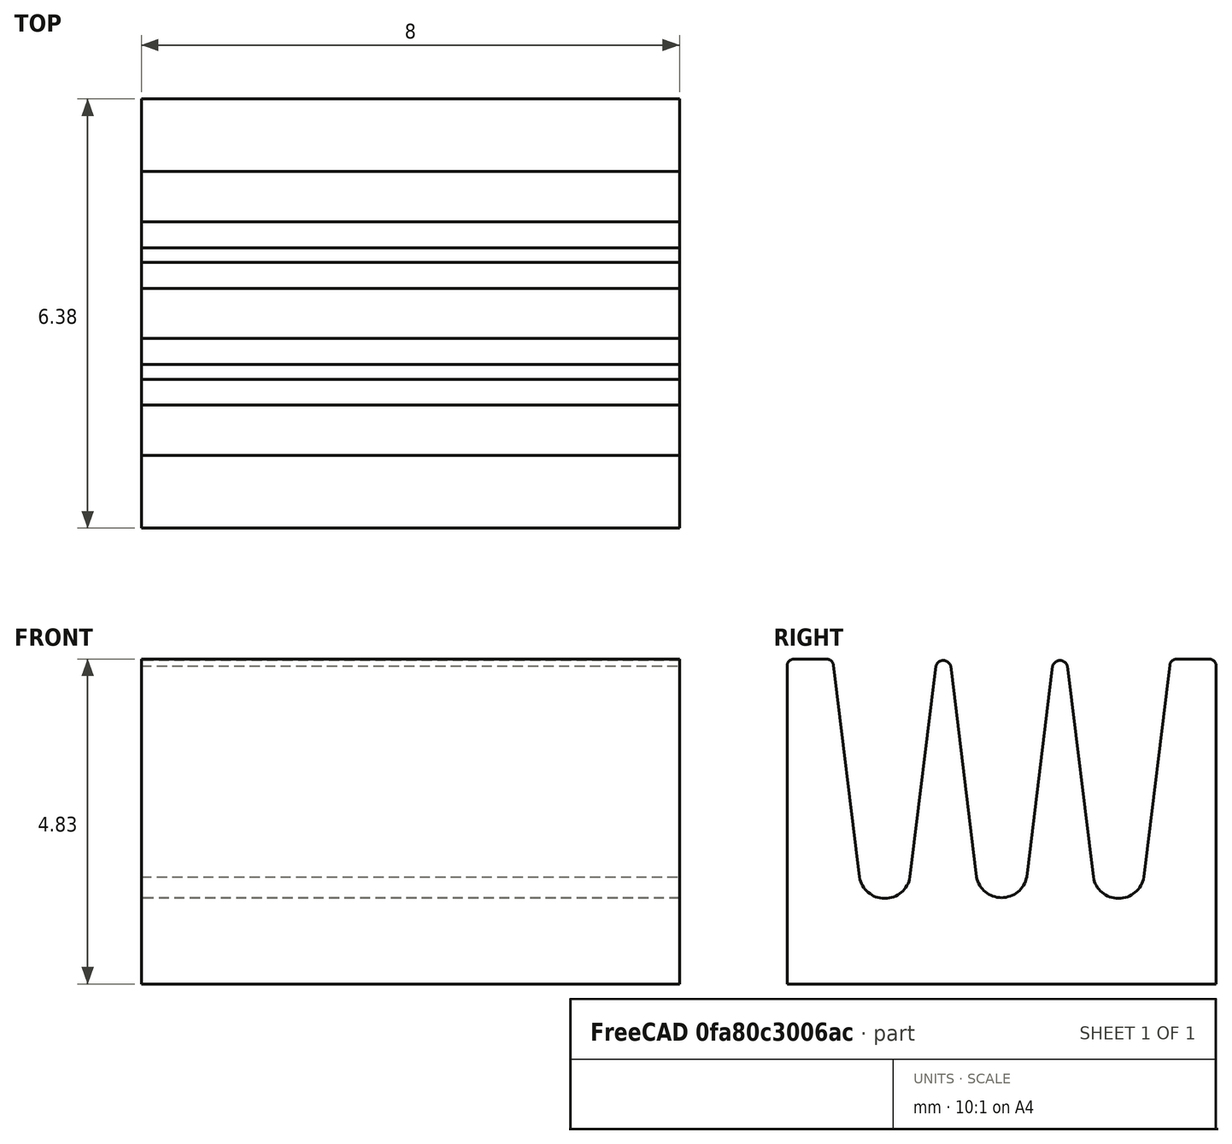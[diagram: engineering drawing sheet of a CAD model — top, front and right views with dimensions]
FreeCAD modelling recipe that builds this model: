
FCSTD DOCUMENT  (FreeCAD 0.18R4 (GitTag))
Label: heat-sink-8x6x5mm
License: CC-BY 3.0
LicenseURL: http://creativecommons.org/licenses/by/3.0/
objects: Sketcher::SketchObject×1, PartDesign::Pad×1, PartDesign::Body×1, App::Part×1
note: 4 computed .brp shape members not serialized (recipe doc carries the construction recipe); baked Part::Feature solids carry a one-line shape summary decoded from their .brp

FEATURE [Sketcher::SketchObject] Sketch  label="heat-sink-sketch"
  MapMode = 5
  Placement = pos=(0,0,0) rot=(0.57735,0.57735,0.57735;2.0944rad)
  Support = -> [YZ_Plane001]
  sketch-geometry (25):
    g0: LineSegment StartX=3.19 StartY=0 StartZ=0 EndX=-3.19 EndY=0 EndZ=0
    g1: LineSegment [constr] StartX=-3.18796 StartY=1.26 StartZ=0 EndX=0 EndY=1.26 EndZ=0
    g2: LineSegment [constr] StartX=-2.59925 StartY=4.83 StartZ=0 EndX=0 EndY=4.83 EndZ=0
    g3: LineSegment [constr] StartX=-1.73796 StartY=4.83 StartZ=0 EndX=-1.73796 EndY=1.26 EndZ=0
    g4: LineSegment [constr] StartX=-0.86796 StartY=4.83 StartZ=0 EndX=-0.86796 EndY=1.26 EndZ=0
    g5: LineSegment [constr] StartX=-2.11296 StartY=1.59 StartZ=0 EndX=-1.36296 EndY=1.59 EndZ=0
    g6: LineSegment StartX=-2.5 StartY=4.74219 StartZ=0 EndX=-2.11296 EndY=1.59 EndZ=0
    g7: LineSegment StartX=-0.97796 StartY=4.72557 StartZ=0 EndX=-1.36296 EndY=1.59 EndZ=0
    g8: LineSegment StartX=-0.75796 StartY=4.72557 StartZ=0 EndX=-0.37296 EndY=1.59 EndZ=0
    g9: LineSegment StartX=0.75796 StartY=4.72557 StartZ=0 EndX=0.37296 EndY=1.59 EndZ=0
    g10: ArcOfCircle CenterX=-1.73796 CenterY=1.65144 CenterZ=0 NormalX=0 NormalY=0 NormalZ=1 AngleXU=0 Radius=0.38 StartAngle=3.30399 EndAngle=6.12079
    g11: ArcOfCircle CenterX=-0.86796 CenterY=4.69564 CenterZ=0 NormalX=0 NormalY=0 NormalZ=1 AngleXU=0 Radius=0.114 StartAngle=0.265687 EndAngle=2.87591
    g12: LineSegment StartX=-3.19 StartY=0 StartZ=0 EndX=-3.19 EndY=4.73 EndZ=0
    g13: LineSegment StartX=-3.09 StartY=4.83 StartZ=0 EndX=-2.59925 EndY=4.83 EndZ=0
    g14: ArcOfCircle CenterX=-3.09 CenterY=4.73 CenterZ=0 NormalX=0 NormalY=0 NormalZ=1 AngleXU=0 Radius=0.1 StartAngle=1.5708 EndAngle=3.14159
    g15: ArcOfCircle CenterX=-2.59925 CenterY=4.73 CenterZ=0 NormalX=0 NormalY=0 NormalZ=1 AngleXU=0 Radius=0.1 StartAngle=0.122173 EndAngle=1.5708
    g16: ArcOfCircle CenterX=0 CenterY=1.66281 CenterZ=0 NormalX=0 NormalY=0 NormalZ=1 AngleXU=0 Radius=0.38 StartAngle=3.33438 EndAngle=6.0904
    g17: LineSegment StartX=0.97796 StartY=4.72557 StartZ=0 EndX=1.36296 EndY=1.59 EndZ=0
    g18: LineSegment StartX=2.11296 StartY=1.59 StartZ=0 EndX=2.5 EndY=4.74219 EndZ=0
    g19: LineSegment StartX=3.19 StartY=4.73 StartZ=0 EndX=3.19 EndY=0 EndZ=0
    g20: LineSegment StartX=2.59925 StartY=4.83 StartZ=0 EndX=3.09 EndY=4.83 EndZ=0
    g21: ArcOfCircle CenterX=0.86796 CenterY=4.69564 CenterZ=0 NormalX=0 NormalY=0 NormalZ=1 AngleXU=0 Radius=0.114 StartAngle=0.265687 EndAngle=2.87591
    g22: ArcOfCircle CenterX=1.73796 CenterY=1.65144 CenterZ=0 NormalX=0 NormalY=0 NormalZ=1 AngleXU=0 Radius=0.38 StartAngle=3.30399 EndAngle=6.12079
    g23: ArcOfCircle CenterX=2.59925 CenterY=4.73 CenterZ=0 NormalX=0 NormalY=0 NormalZ=1 AngleXU=0 Radius=0.1 StartAngle=1.5708 EndAngle=3.01942
    g24: ArcOfCircle CenterX=3.09 CenterY=4.73 CenterZ=0 NormalX=0 NormalY=0 NormalZ=1 AngleXU=0 Radius=0.1 StartAngle=0 EndAngle=1.5708
  constraints (69):
    c: Symmetric(g0,g0,g-2)
    c: PointOnObject(g0,g-1)
    c: DistanceX(g0) = -6.38
    c: Horizontal(g1)
    c: PointOnObject(g1,g-2)
    c: DistanceY(g-1,g1) = 1.26
    c: PointOnObject(g2,g-2)
    c: PointOnObject(g3,g2)
    c: PointOnObject(g3,g1)
    c: DistanceX(g1,g3) = 1.45
    c: PointOnObject(g4,g1)
    c: PointOnObject(g4,g2)
    c: DistanceX(g3,g4) = 0.87
    c: DistanceX(g3,g4) = 0.87
    c: Horizontal(g5)
    c: Angle(g6,g2) = 1.44862
    c: Angle(g2,g7) = 1.44862
    c: Coincident(g5,g7)
    c: Coincident(g5,g6)
    c: Symmetric(g5,g5,g3)
    c: DistanceX(g5) = 0.75
    c: DistanceY(g5,g4) = -0.33
    c: Parallel(g8,g6)
    c: Symmetric(g7,g8,g4)
    c: DistanceX(g7,g8) = 0.22
    c: Symmetric(g8,g5,g4)
    c: Symmetric(g8,g9,g-2)
    c: Symmetric(g9,g8,g-2)
    c: Coincident(g10,g5)
    c: Coincident(g10,g5)
    c: Radius(g10) = 0.38
    c: Coincident(g11,g7)
    c: Coincident(g11,g8)
    c: Radius(g11) = 0.114
    c: DistanceY(g2,g0) = -4.83
    c: Vertical(g12)
    c: Horizontal(g13)
    c: Coincident(g12,g0)
    c: Tangent(g12,g14)
    c: Tangent(g13,g14)
    c: Radius(g14) = 0.1
    c: Tangent(g6,g15)
    c: Tangent(g13,g15)
    c: Equal(g15,g14)
    c: DistanceX(g12,g6) = 0.69
    c: Coincident(g2,g13)
    c: Coincident(g16,g8)
    c: Coincident(g16,g9)
    c: Equal(g10,g16)
    c: Symmetric(g5,g17,g-2)
    c: Symmetric(g17,g7,g-2)
    c: Symmetric(g18,g6,g-2)
    c: Symmetric(g18,g5,g-2)
    c: Coincident(g19,g0)
    c: Symmetric(g19,g12,g-2)
    c: Symmetric(g20,g2,g-2)
    c: Symmetric(g20,g13,g-2)
    c: Coincident(g21,g9)
    c: Coincident(g17,g21)
    c: Equal(g21,g11)
    c: Equal(g22,g16)
    c: Coincident(g22,g17)
    c: Coincident(g22,g18)
    c: Equal(g23,g14)
    c: Coincident(g23,g18)
    c: Coincident(g23,g20)
    c: Coincident(g24,g20)
    c: Coincident(g24,g19)
    c: Equal(g24,g23)
FEATURE [PartDesign::Pad] Pad  label="heat-sink-8x6x5mm"
  Length = 8
  Length2 = 100
  Midplane = true
  Placement = pos=(0,0,0) rot=(0.57735,0.57735,0.57735;2.0944rad)
  Profile = -> Sketch
  Refine = true
  Type = 0
FEATURE [PartDesign::Body] PadBody
  Group = -> [Sketch,Pad]
  Origin = -> Origin001
  Tip = -> Pad
FEATURE [App::Part] Part
  Group = -> [PadBody]
  Origin = -> Origin
